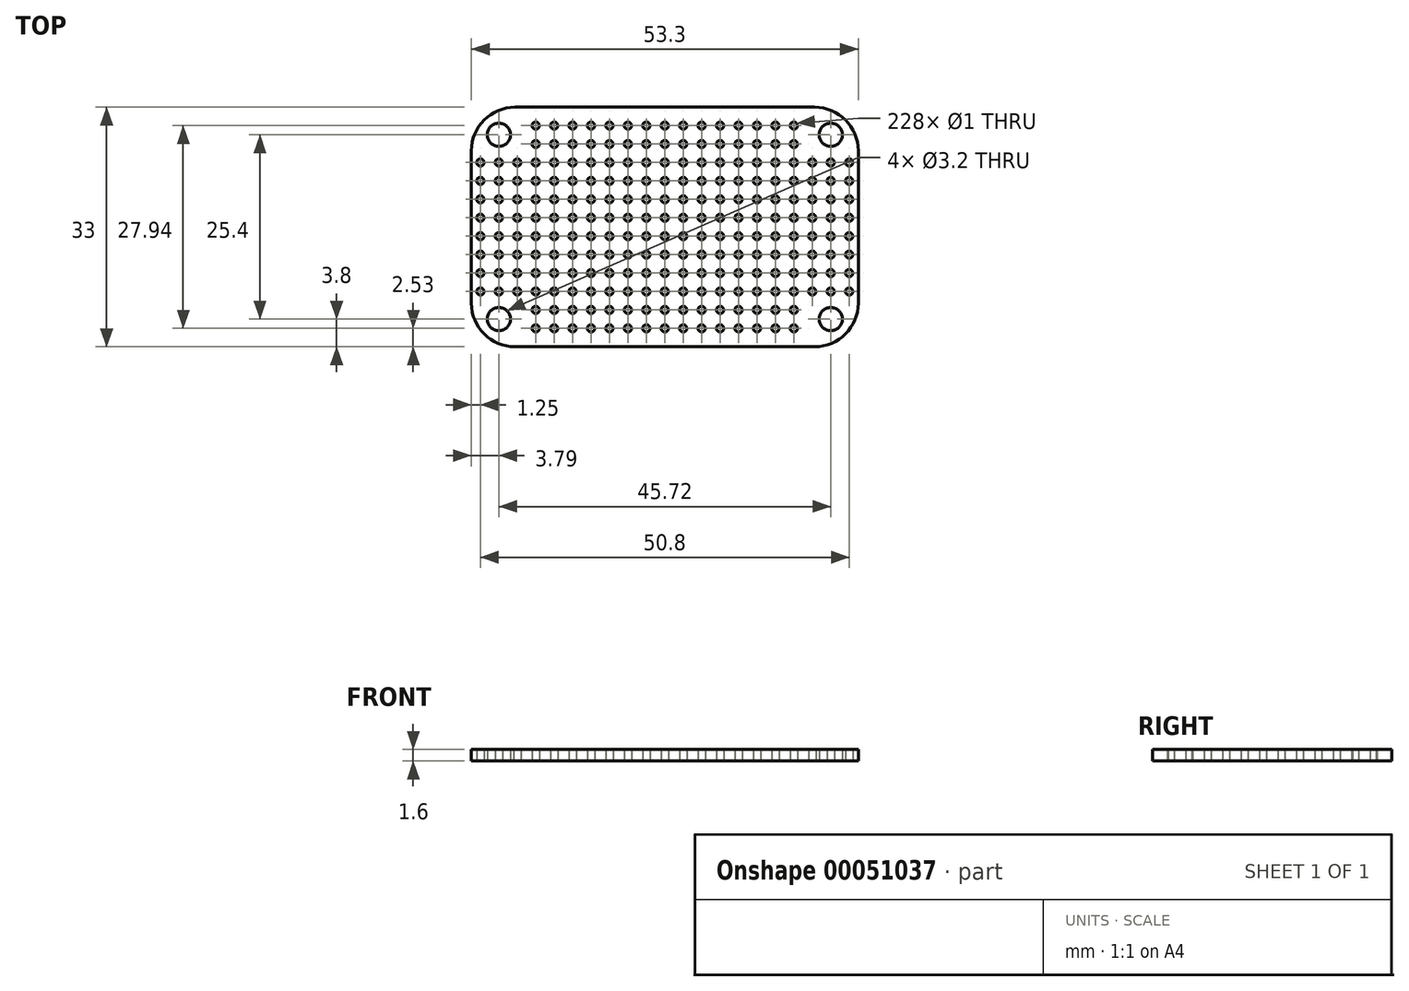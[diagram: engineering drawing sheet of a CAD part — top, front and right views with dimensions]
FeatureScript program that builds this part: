
annotation { "Feature Type Name" : "Feature", "Feature Type Description" : "" }
export const myFeature = defineFeature(function(context is Context, id is Id, definition is map)
    precondition{}
    {
        {
            var Q0;
            Q0=qCreatedBy(makeId("Top.planeOp"),FACE);
            var sketch = newSketch(context, id + "F0", { "sketchPlane" : qUnion([Q0])});
            skLineSegment(sketch, "E0.rect.bottom", {"start": v(20.65, -16.5) * mm, "end": v(-20.65, -16.5) * mm});
            skLineSegment(sketch, "E0.rect.top", {"start": v(20.65, 16.5) * mm, "end": v(-20.65, 16.5) * mm});
            skLineSegment(sketch, "E0.rect.left", {"start": v(26.65, -10.5) * mm, "end": v(26.65, 10.5) * mm});
            skLineSegment(sketch, "E0.rect.right", {"start": v(-26.65, -10.5) * mm, "end": v(-26.65, 10.5) * mm});
            skPoint(sketch, "E0.rect.middle", {"position": v(0, 0) * mm});
            skCircle(sketch, "E1.0.2.0", {"center": v(-25.4, 8.9) * mm, "radius": 0.5 * mm});
            skCircle(sketch, "E1.0.3.0", {"center": v(-25.4, 6.35) * mm, "radius": 0.5 * mm});
            skCircle(sketch, "E1.0.4.0", {"center": v(-25.4, 3.81) * mm, "radius": 0.5 * mm});
            skCircle(sketch, "E1.0.5.0", {"center": v(-25.4, 1.27) * mm, "radius": 0.5 * mm});
            skCircle(sketch, "E1.0.6.0", {"center": v(-25.4, -1.27) * mm, "radius": 0.5 * mm});
            skCircle(sketch, "E1.0.7.0", {"center": v(-25.4, -3.81) * mm, "radius": 0.5 * mm});
            skCircle(sketch, "E1.0.8.0", {"center": v(-25.4, -6.35) * mm, "radius": 0.5 * mm});
            skCircle(sketch, "E1.0.9.0", {"center": v(-25.4, -8.9) * mm, "radius": 0.5 * mm});
            skCircle(sketch, "E1.1.2.0", {"center": v(-22.86, 8.9) * mm, "radius": 0.5 * mm});
            skCircle(sketch, "E1.1.3.0", {"center": v(-22.86, 6.35) * mm, "radius": 0.5 * mm});
            skCircle(sketch, "E1.1.4.0", {"center": v(-22.86, 3.81) * mm, "radius": 0.5 * mm});
            skCircle(sketch, "E1.1.5.0", {"center": v(-22.86, 1.27) * mm, "radius": 0.5 * mm});
            skCircle(sketch, "E1.1.6.0", {"center": v(-22.86, -1.27) * mm, "radius": 0.5 * mm});
            skCircle(sketch, "E1.1.7.0", {"center": v(-22.86, -3.81) * mm, "radius": 0.5 * mm});
            skCircle(sketch, "E1.1.8.0", {"center": v(-22.86, -6.35) * mm, "radius": 0.5 * mm});
            skCircle(sketch, "E1.1.9.0", {"center": v(-22.86, -8.9) * mm, "radius": 0.5 * mm});
            skCircle(sketch, "E1.2.2.0", {"center": v(-20.32, 8.9) * mm, "radius": 0.5 * mm});
            skCircle(sketch, "E1.2.3.0", {"center": v(-20.32, 6.35) * mm, "radius": 0.5 * mm});
            skCircle(sketch, "E1.2.4.0", {"center": v(-20.32, 3.81) * mm, "radius": 0.5 * mm});
            skCircle(sketch, "E1.2.5.0", {"center": v(-20.32, 1.27) * mm, "radius": 0.5 * mm});
            skCircle(sketch, "E1.2.6.0", {"center": v(-20.32, -1.27) * mm, "radius": 0.5 * mm});
            skCircle(sketch, "E1.2.7.0", {"center": v(-20.32, -3.81) * mm, "radius": 0.5 * mm});
            skCircle(sketch, "E1.2.8.0", {"center": v(-20.32, -6.35) * mm, "radius": 0.5 * mm});
            skCircle(sketch, "E1.2.9.0", {"center": v(-20.32, -8.9) * mm, "radius": 0.5 * mm});
            skCircle(sketch, "E1.3.0.0", {"center": v(-17.78, 13.97) * mm, "radius": 0.5 * mm});
            skCircle(sketch, "E1.3.1.0", {"center": v(-17.78, 11.43) * mm, "radius": 0.5 * mm});
            skCircle(sketch, "E1.3.2.0", {"center": v(-17.78, 8.9) * mm, "radius": 0.5 * mm});
            skCircle(sketch, "E1.3.3.0", {"center": v(-17.78, 6.35) * mm, "radius": 0.5 * mm});
            skCircle(sketch, "E1.3.4.0", {"center": v(-17.78, 3.81) * mm, "radius": 0.5 * mm});
            skCircle(sketch, "E1.3.5.0", {"center": v(-17.78, 1.27) * mm, "radius": 0.5 * mm});
            skCircle(sketch, "E1.3.6.0", {"center": v(-17.78, -1.27) * mm, "radius": 0.5 * mm});
            skCircle(sketch, "E1.3.7.0", {"center": v(-17.78, -3.81) * mm, "radius": 0.5 * mm});
            skCircle(sketch, "E1.3.8.0", {"center": v(-17.78, -6.35) * mm, "radius": 0.5 * mm});
            skCircle(sketch, "E1.3.9.0", {"center": v(-17.78, -8.9) * mm, "radius": 0.5 * mm});
            skCircle(sketch, "E1.3.10.0", {"center": v(-17.78, -11.43) * mm, "radius": 0.5 * mm});
            skCircle(sketch, "E1.3.11.0", {"center": v(-17.78, -13.97) * mm, "radius": 0.5 * mm});
            skCircle(sketch, "E1.4.0.0", {"center": v(-15.24, 13.97) * mm, "radius": 0.5 * mm});
            skCircle(sketch, "E1.4.1.0", {"center": v(-15.24, 11.43) * mm, "radius": 0.5 * mm});
            skCircle(sketch, "E1.4.2.0", {"center": v(-15.24, 8.9) * mm, "radius": 0.5 * mm});
            skCircle(sketch, "E1.4.3.0", {"center": v(-15.24, 6.35) * mm, "radius": 0.5 * mm});
            skCircle(sketch, "E1.4.4.0", {"center": v(-15.24, 3.81) * mm, "radius": 0.5 * mm});
            skCircle(sketch, "E1.4.5.0", {"center": v(-15.24, 1.27) * mm, "radius": 0.5 * mm});
            skCircle(sketch, "E1.4.6.0", {"center": v(-15.24, -1.27) * mm, "radius": 0.5 * mm});
            skCircle(sketch, "E1.4.7.0", {"center": v(-15.24, -3.81) * mm, "radius": 0.5 * mm});
            skCircle(sketch, "E1.4.8.0", {"center": v(-15.24, -6.35) * mm, "radius": 0.5 * mm});
            skCircle(sketch, "E1.4.9.0", {"center": v(-15.24, -8.9) * mm, "radius": 0.5 * mm});
            skCircle(sketch, "E1.4.10.0", {"center": v(-15.24, -11.43) * mm, "radius": 0.5 * mm});
            skCircle(sketch, "E1.4.11.0", {"center": v(-15.24, -13.97) * mm, "radius": 0.5 * mm});
            skCircle(sketch, "E1.5.0.0", {"center": v(-12.7, 13.97) * mm, "radius": 0.5 * mm});
            skCircle(sketch, "E1.5.1.0", {"center": v(-12.7, 11.43) * mm, "radius": 0.5 * mm});
            skCircle(sketch, "E1.5.2.0", {"center": v(-12.7, 8.9) * mm, "radius": 0.5 * mm});
            skCircle(sketch, "E1.5.3.0", {"center": v(-12.7, 6.35) * mm, "radius": 0.5 * mm});
            skCircle(sketch, "E1.5.4.0", {"center": v(-12.7, 3.81) * mm, "radius": 0.5 * mm});
            skCircle(sketch, "E1.5.5.0", {"center": v(-12.7, 1.27) * mm, "radius": 0.5 * mm});
            skCircle(sketch, "E1.5.6.0", {"center": v(-12.7, -1.27) * mm, "radius": 0.5 * mm});
            skCircle(sketch, "E1.5.7.0", {"center": v(-12.7, -3.81) * mm, "radius": 0.5 * mm});
            skCircle(sketch, "E1.5.8.0", {"center": v(-12.7, -6.35) * mm, "radius": 0.5 * mm});
            skCircle(sketch, "E1.5.9.0", {"center": v(-12.7, -8.9) * mm, "radius": 0.5 * mm});
            skCircle(sketch, "E1.5.10.0", {"center": v(-12.7, -11.43) * mm, "radius": 0.5 * mm});
            skCircle(sketch, "E1.5.11.0", {"center": v(-12.7, -13.97) * mm, "radius": 0.5 * mm});
            skCircle(sketch, "E1.6.0.0", {"center": v(-10.16, 13.97) * mm, "radius": 0.5 * mm});
            skCircle(sketch, "E1.6.1.0", {"center": v(-10.16, 11.43) * mm, "radius": 0.5 * mm});
            skCircle(sketch, "E1.6.2.0", {"center": v(-10.16, 8.9) * mm, "radius": 0.5 * mm});
            skCircle(sketch, "E1.6.3.0", {"center": v(-10.16, 6.35) * mm, "radius": 0.5 * mm});
            skCircle(sketch, "E1.6.4.0", {"center": v(-10.16, 3.81) * mm, "radius": 0.5 * mm});
            skCircle(sketch, "E1.6.5.0", {"center": v(-10.16, 1.27) * mm, "radius": 0.5 * mm});
            skCircle(sketch, "E1.6.6.0", {"center": v(-10.16, -1.27) * mm, "radius": 0.5 * mm});
            skCircle(sketch, "E1.6.7.0", {"center": v(-10.16, -3.81) * mm, "radius": 0.5 * mm});
            skCircle(sketch, "E1.6.8.0", {"center": v(-10.16, -6.35) * mm, "radius": 0.5 * mm});
            skCircle(sketch, "E1.6.9.0", {"center": v(-10.16, -8.9) * mm, "radius": 0.5 * mm});
            skCircle(sketch, "E1.6.10.0", {"center": v(-10.16, -11.43) * mm, "radius": 0.5 * mm});
            skCircle(sketch, "E1.6.11.0", {"center": v(-10.16, -13.97) * mm, "radius": 0.5 * mm});
            skCircle(sketch, "E1.7.0.0", {"center": v(-7.62, 13.97) * mm, "radius": 0.5 * mm});
            skCircle(sketch, "E1.7.1.0", {"center": v(-7.62, 11.43) * mm, "radius": 0.5 * mm});
            skCircle(sketch, "E1.7.2.0", {"center": v(-7.62, 8.9) * mm, "radius": 0.5 * mm});
            skCircle(sketch, "E1.7.3.0", {"center": v(-7.62, 6.35) * mm, "radius": 0.5 * mm});
            skCircle(sketch, "E1.7.4.0", {"center": v(-7.62, 3.81) * mm, "radius": 0.5 * mm});
            skCircle(sketch, "E1.7.5.0", {"center": v(-7.62, 1.27) * mm, "radius": 0.5 * mm});
            skCircle(sketch, "E1.7.6.0", {"center": v(-7.62, -1.27) * mm, "radius": 0.5 * mm});
            skCircle(sketch, "E1.7.7.0", {"center": v(-7.62, -3.81) * mm, "radius": 0.5 * mm});
            skCircle(sketch, "E1.7.8.0", {"center": v(-7.62, -6.35) * mm, "radius": 0.5 * mm});
            skCircle(sketch, "E1.7.9.0", {"center": v(-7.62, -8.9) * mm, "radius": 0.5 * mm});
            skCircle(sketch, "E1.7.10.0", {"center": v(-7.62, -11.43) * mm, "radius": 0.5 * mm});
            skCircle(sketch, "E1.7.11.0", {"center": v(-7.62, -13.97) * mm, "radius": 0.5 * mm});
            skCircle(sketch, "E1.8.0.0", {"center": v(-5.08, 13.97) * mm, "radius": 0.5 * mm});
            skCircle(sketch, "E1.8.1.0", {"center": v(-5.08, 11.43) * mm, "radius": 0.5 * mm});
            skCircle(sketch, "E1.8.2.0", {"center": v(-5.08, 8.9) * mm, "radius": 0.5 * mm});
            skCircle(sketch, "E1.8.3.0", {"center": v(-5.08, 6.35) * mm, "radius": 0.5 * mm});
            skCircle(sketch, "E1.8.4.0", {"center": v(-5.08, 3.81) * mm, "radius": 0.5 * mm});
            skCircle(sketch, "E1.8.5.0", {"center": v(-5.08, 1.27) * mm, "radius": 0.5 * mm});
            skCircle(sketch, "E1.8.6.0", {"center": v(-5.08, -1.27) * mm, "radius": 0.5 * mm});
            skCircle(sketch, "E1.8.7.0", {"center": v(-5.08, -3.81) * mm, "radius": 0.5 * mm});
            skCircle(sketch, "E1.8.8.0", {"center": v(-5.08, -6.35) * mm, "radius": 0.5 * mm});
            skCircle(sketch, "E1.8.9.0", {"center": v(-5.08, -8.9) * mm, "radius": 0.5 * mm});
            skCircle(sketch, "E1.8.10.0", {"center": v(-5.08, -11.43) * mm, "radius": 0.5 * mm});
            skCircle(sketch, "E1.8.11.0", {"center": v(-5.08, -13.97) * mm, "radius": 0.5 * mm});
            skCircle(sketch, "E1.9.0.0", {"center": v(-2.54, 13.97) * mm, "radius": 0.5 * mm});
            skCircle(sketch, "E1.9.1.0", {"center": v(-2.54, 11.43) * mm, "radius": 0.5 * mm});
            skCircle(sketch, "E1.9.2.0", {"center": v(-2.54, 8.9) * mm, "radius": 0.5 * mm});
            skCircle(sketch, "E1.9.3.0", {"center": v(-2.54, 6.35) * mm, "radius": 0.5 * mm});
            skCircle(sketch, "E1.9.4.0", {"center": v(-2.54, 3.81) * mm, "radius": 0.5 * mm});
            skCircle(sketch, "E1.9.5.0", {"center": v(-2.54, 1.27) * mm, "radius": 0.5 * mm});
            skCircle(sketch, "E1.9.6.0", {"center": v(-2.54, -1.27) * mm, "radius": 0.5 * mm});
            skCircle(sketch, "E1.9.7.0", {"center": v(-2.54, -3.81) * mm, "radius": 0.5 * mm});
            skCircle(sketch, "E1.9.8.0", {"center": v(-2.54, -6.35) * mm, "radius": 0.5 * mm});
            skCircle(sketch, "E1.9.9.0", {"center": v(-2.54, -8.9) * mm, "radius": 0.5 * mm});
            skCircle(sketch, "E1.9.10.0", {"center": v(-2.54, -11.43) * mm, "radius": 0.5 * mm});
            skCircle(sketch, "E1.9.11.0", {"center": v(-2.54, -13.97) * mm, "radius": 0.5 * mm});
            skCircle(sketch, "E1.10.0.0", {"center": v(0, 13.97) * mm, "radius": 0.5 * mm});
            skCircle(sketch, "E1.10.1.0", {"center": v(0, 11.43) * mm, "radius": 0.5 * mm});
            skCircle(sketch, "E1.10.2.0", {"center": v(0, 8.9) * mm, "radius": 0.5 * mm});
            skCircle(sketch, "E1.10.3.0", {"center": v(0, 6.35) * mm, "radius": 0.5 * mm});
            skCircle(sketch, "E1.10.4.0", {"center": v(0, 3.81) * mm, "radius": 0.5 * mm});
            skCircle(sketch, "E1.10.5.0", {"center": v(0, 1.27) * mm, "radius": 0.5 * mm});
            skCircle(sketch, "E1.10.6.0", {"center": v(0, -1.27) * mm, "radius": 0.5 * mm});
            skCircle(sketch, "E1.10.7.0", {"center": v(0, -3.81) * mm, "radius": 0.5 * mm});
            skCircle(sketch, "E1.10.8.0", {"center": v(0, -6.35) * mm, "radius": 0.5 * mm});
            skCircle(sketch, "E1.10.9.0", {"center": v(0, -8.9) * mm, "radius": 0.5 * mm});
            skCircle(sketch, "E1.10.10.0", {"center": v(0, -11.43) * mm, "radius": 0.5 * mm});
            skCircle(sketch, "E1.10.11.0", {"center": v(0, -13.97) * mm, "radius": 0.5 * mm});
            skCircle(sketch, "E1.11.0.0", {"center": v(2.54, 13.97) * mm, "radius": 0.5 * mm});
            skCircle(sketch, "E1.11.1.0", {"center": v(2.54, 11.43) * mm, "radius": 0.5 * mm});
            skCircle(sketch, "E1.11.2.0", {"center": v(2.54, 8.9) * mm, "radius": 0.5 * mm});
            skCircle(sketch, "E1.11.3.0", {"center": v(2.54, 6.35) * mm, "radius": 0.5 * mm});
            skCircle(sketch, "E1.11.4.0", {"center": v(2.54, 3.81) * mm, "radius": 0.5 * mm});
            skCircle(sketch, "E1.11.5.0", {"center": v(2.54, 1.27) * mm, "radius": 0.5 * mm});
            skCircle(sketch, "E1.11.6.0", {"center": v(2.54, -1.27) * mm, "radius": 0.5 * mm});
            skCircle(sketch, "E1.11.7.0", {"center": v(2.54, -3.81) * mm, "radius": 0.5 * mm});
            skCircle(sketch, "E1.11.8.0", {"center": v(2.54, -6.35) * mm, "radius": 0.5 * mm});
            skCircle(sketch, "E1.11.9.0", {"center": v(2.54, -8.9) * mm, "radius": 0.5 * mm});
            skCircle(sketch, "E1.11.10.0", {"center": v(2.54, -11.43) * mm, "radius": 0.5 * mm});
            skCircle(sketch, "E1.11.11.0", {"center": v(2.54, -13.97) * mm, "radius": 0.5 * mm});
            skCircle(sketch, "E1.12.0.0", {"center": v(5.08, 13.97) * mm, "radius": 0.5 * mm});
            skCircle(sketch, "E1.12.1.0", {"center": v(5.08, 11.43) * mm, "radius": 0.5 * mm});
            skCircle(sketch, "E1.12.2.0", {"center": v(5.08, 8.9) * mm, "radius": 0.5 * mm});
            skCircle(sketch, "E1.12.3.0", {"center": v(5.08, 6.35) * mm, "radius": 0.5 * mm});
            skCircle(sketch, "E1.12.4.0", {"center": v(5.08, 3.81) * mm, "radius": 0.5 * mm});
            skCircle(sketch, "E1.12.5.0", {"center": v(5.08, 1.27) * mm, "radius": 0.5 * mm});
            skCircle(sketch, "E1.12.6.0", {"center": v(5.08, -1.27) * mm, "radius": 0.5 * mm});
            skCircle(sketch, "E1.12.7.0", {"center": v(5.08, -3.81) * mm, "radius": 0.5 * mm});
            skCircle(sketch, "E1.12.8.0", {"center": v(5.08, -6.35) * mm, "radius": 0.5 * mm});
            skCircle(sketch, "E1.12.9.0", {"center": v(5.08, -8.9) * mm, "radius": 0.5 * mm});
            skCircle(sketch, "E1.12.10.0", {"center": v(5.08, -11.43) * mm, "radius": 0.5 * mm});
            skCircle(sketch, "E1.12.11.0", {"center": v(5.08, -13.97) * mm, "radius": 0.5 * mm});
            skCircle(sketch, "E1.13.0.0", {"center": v(7.62, 13.97) * mm, "radius": 0.5 * mm});
            skCircle(sketch, "E1.13.1.0", {"center": v(7.62, 11.43) * mm, "radius": 0.5 * mm});
            skCircle(sketch, "E1.13.2.0", {"center": v(7.62, 8.9) * mm, "radius": 0.5 * mm});
            skCircle(sketch, "E1.13.3.0", {"center": v(7.62, 6.35) * mm, "radius": 0.5 * mm});
            skCircle(sketch, "E1.13.4.0", {"center": v(7.62, 3.81) * mm, "radius": 0.5 * mm});
            skCircle(sketch, "E1.13.5.0", {"center": v(7.62, 1.27) * mm, "radius": 0.5 * mm});
            skCircle(sketch, "E1.13.6.0", {"center": v(7.62, -1.27) * mm, "radius": 0.5 * mm});
            skCircle(sketch, "E1.13.7.0", {"center": v(7.62, -3.81) * mm, "radius": 0.5 * mm});
            skCircle(sketch, "E1.13.8.0", {"center": v(7.62, -6.35) * mm, "radius": 0.5 * mm});
            skCircle(sketch, "E1.13.9.0", {"center": v(7.62, -8.9) * mm, "radius": 0.5 * mm});
            skCircle(sketch, "E1.13.10.0", {"center": v(7.62, -11.43) * mm, "radius": 0.5 * mm});
            skCircle(sketch, "E1.13.11.0", {"center": v(7.62, -13.97) * mm, "radius": 0.5 * mm});
            skCircle(sketch, "E1.14.0.0", {"center": v(10.16, 13.97) * mm, "radius": 0.5 * mm});
            skCircle(sketch, "E1.14.1.0", {"center": v(10.16, 11.43) * mm, "radius": 0.5 * mm});
            skCircle(sketch, "E1.14.2.0", {"center": v(10.16, 8.9) * mm, "radius": 0.5 * mm});
            skCircle(sketch, "E1.14.3.0", {"center": v(10.16, 6.35) * mm, "radius": 0.5 * mm});
            skCircle(sketch, "E1.14.4.0", {"center": v(10.16, 3.81) * mm, "radius": 0.5 * mm});
            skCircle(sketch, "E1.14.5.0", {"center": v(10.16, 1.27) * mm, "radius": 0.5 * mm});
            skCircle(sketch, "E1.14.6.0", {"center": v(10.16, -1.27) * mm, "radius": 0.5 * mm});
            skCircle(sketch, "E1.14.7.0", {"center": v(10.16, -3.81) * mm, "radius": 0.5 * mm});
            skCircle(sketch, "E1.14.8.0", {"center": v(10.16, -6.35) * mm, "radius": 0.5 * mm});
            skCircle(sketch, "E1.14.9.0", {"center": v(10.16, -8.9) * mm, "radius": 0.5 * mm});
            skCircle(sketch, "E1.14.10.0", {"center": v(10.16, -11.43) * mm, "radius": 0.5 * mm});
            skCircle(sketch, "E1.14.11.0", {"center": v(10.16, -13.97) * mm, "radius": 0.5 * mm});
            skCircle(sketch, "E1.15.0.0", {"center": v(12.7, 13.97) * mm, "radius": 0.5 * mm});
            skCircle(sketch, "E1.15.1.0", {"center": v(12.7, 11.43) * mm, "radius": 0.5 * mm});
            skCircle(sketch, "E1.15.2.0", {"center": v(12.7, 8.9) * mm, "radius": 0.5 * mm});
            skCircle(sketch, "E1.15.3.0", {"center": v(12.7, 6.35) * mm, "radius": 0.5 * mm});
            skCircle(sketch, "E1.15.4.0", {"center": v(12.7, 3.81) * mm, "radius": 0.5 * mm});
            skCircle(sketch, "E1.15.5.0", {"center": v(12.7, 1.27) * mm, "radius": 0.5 * mm});
            skCircle(sketch, "E1.15.6.0", {"center": v(12.7, -1.27) * mm, "radius": 0.5 * mm});
            skCircle(sketch, "E1.15.7.0", {"center": v(12.7, -3.81) * mm, "radius": 0.5 * mm});
            skCircle(sketch, "E1.15.8.0", {"center": v(12.7, -6.35) * mm, "radius": 0.5 * mm});
            skCircle(sketch, "E1.15.9.0", {"center": v(12.7, -8.9) * mm, "radius": 0.5 * mm});
            skCircle(sketch, "E1.15.10.0", {"center": v(12.7, -11.43) * mm, "radius": 0.5 * mm});
            skCircle(sketch, "E1.15.11.0", {"center": v(12.7, -13.97) * mm, "radius": 0.5 * mm});
            skCircle(sketch, "E1.16.0.0", {"center": v(15.24, 13.97) * mm, "radius": 0.5 * mm});
            skCircle(sketch, "E1.16.1.0", {"center": v(15.24, 11.43) * mm, "radius": 0.5 * mm});
            skCircle(sketch, "E1.16.2.0", {"center": v(15.24, 8.9) * mm, "radius": 0.5 * mm});
            skCircle(sketch, "E1.16.3.0", {"center": v(15.24, 6.35) * mm, "radius": 0.5 * mm});
            skCircle(sketch, "E1.16.4.0", {"center": v(15.24, 3.81) * mm, "radius": 0.5 * mm});
            skCircle(sketch, "E1.16.5.0", {"center": v(15.24, 1.27) * mm, "radius": 0.5 * mm});
            skCircle(sketch, "E1.16.6.0", {"center": v(15.24, -1.27) * mm, "radius": 0.5 * mm});
            skCircle(sketch, "E1.16.7.0", {"center": v(15.24, -3.81) * mm, "radius": 0.5 * mm});
            skCircle(sketch, "E1.16.8.0", {"center": v(15.24, -6.35) * mm, "radius": 0.5 * mm});
            skCircle(sketch, "E1.16.9.0", {"center": v(15.24, -8.9) * mm, "radius": 0.5 * mm});
            skCircle(sketch, "E1.16.10.0", {"center": v(15.24, -11.43) * mm, "radius": 0.5 * mm});
            skCircle(sketch, "E1.16.11.0", {"center": v(15.24, -13.97) * mm, "radius": 0.5 * mm});
            skCircle(sketch, "E1.17.0.0", {"center": v(17.78, 13.97) * mm, "radius": 0.5 * mm});
            skCircle(sketch, "E1.17.1.0", {"center": v(17.78, 11.43) * mm, "radius": 0.5 * mm});
            skCircle(sketch, "E1.17.2.0", {"center": v(17.78, 8.9) * mm, "radius": 0.5 * mm});
            skCircle(sketch, "E1.17.3.0", {"center": v(17.78, 6.35) * mm, "radius": 0.5 * mm});
            skCircle(sketch, "E1.17.4.0", {"center": v(17.78, 3.81) * mm, "radius": 0.5 * mm});
            skCircle(sketch, "E1.17.5.0", {"center": v(17.78, 1.27) * mm, "radius": 0.5 * mm});
            skCircle(sketch, "E1.17.6.0", {"center": v(17.78, -1.27) * mm, "radius": 0.5 * mm});
            skCircle(sketch, "E1.17.7.0", {"center": v(17.78, -3.81) * mm, "radius": 0.5 * mm});
            skCircle(sketch, "E1.17.8.0", {"center": v(17.78, -6.35) * mm, "radius": 0.5 * mm});
            skCircle(sketch, "E1.17.9.0", {"center": v(17.78, -8.9) * mm, "radius": 0.5 * mm});
            skCircle(sketch, "E1.17.10.0", {"center": v(17.78, -11.43) * mm, "radius": 0.5 * mm});
            skCircle(sketch, "E1.17.11.0", {"center": v(17.78, -13.97) * mm, "radius": 0.5 * mm});
            skCircle(sketch, "E1.18.2.0", {"center": v(20.32, 8.9) * mm, "radius": 0.5 * mm});
            skCircle(sketch, "E1.18.3.0", {"center": v(20.32, 6.35) * mm, "radius": 0.5 * mm});
            skCircle(sketch, "E1.18.4.0", {"center": v(20.32, 3.81) * mm, "radius": 0.5 * mm});
            skCircle(sketch, "E1.18.5.0", {"center": v(20.32, 1.27) * mm, "radius": 0.5 * mm});
            skCircle(sketch, "E1.18.6.0", {"center": v(20.32, -1.27) * mm, "radius": 0.5 * mm});
            skCircle(sketch, "E1.18.7.0", {"center": v(20.32, -3.81) * mm, "radius": 0.5 * mm});
            skCircle(sketch, "E1.18.8.0", {"center": v(20.32, -6.35) * mm, "radius": 0.5 * mm});
            skCircle(sketch, "E1.18.9.0", {"center": v(20.32, -8.9) * mm, "radius": 0.5 * mm});
            skCircle(sketch, "E1.19.2.0", {"center": v(22.86, 8.9) * mm, "radius": 0.5 * mm});
            skCircle(sketch, "E1.19.3.0", {"center": v(22.86, 6.35) * mm, "radius": 0.5 * mm});
            skCircle(sketch, "E1.19.4.0", {"center": v(22.86, 3.81) * mm, "radius": 0.5 * mm});
            skCircle(sketch, "E1.19.5.0", {"center": v(22.86, 1.27) * mm, "radius": 0.5 * mm});
            skCircle(sketch, "E1.19.6.0", {"center": v(22.86, -1.27) * mm, "radius": 0.5 * mm});
            skCircle(sketch, "E1.19.7.0", {"center": v(22.86, -3.81) * mm, "radius": 0.5 * mm});
            skCircle(sketch, "E1.19.8.0", {"center": v(22.86, -6.35) * mm, "radius": 0.5 * mm});
            skCircle(sketch, "E1.19.9.0", {"center": v(22.86, -8.9) * mm, "radius": 0.5 * mm});
            skCircle(sketch, "E1.20.2.0", {"center": v(25.4, 8.9) * mm, "radius": 0.5 * mm});
            skCircle(sketch, "E1.20.3.0", {"center": v(25.4, 6.35) * mm, "radius": 0.5 * mm});
            skCircle(sketch, "E1.20.4.0", {"center": v(25.4, 3.81) * mm, "radius": 0.5 * mm});
            skCircle(sketch, "E1.20.5.0", {"center": v(25.4, 1.27) * mm, "radius": 0.5 * mm});
            skCircle(sketch, "E1.20.6.0", {"center": v(25.4, -1.27) * mm, "radius": 0.5 * mm});
            skCircle(sketch, "E1.20.7.0", {"center": v(25.4, -3.81) * mm, "radius": 0.5 * mm});
            skCircle(sketch, "E1.20.8.0", {"center": v(25.4, -6.35) * mm, "radius": 0.5 * mm});
            skCircle(sketch, "E1.20.9.0", {"center": v(25.4, -8.9) * mm, "radius": 0.5 * mm});
            skLineSegment(sketch, "E1.direction1", {"start": v(-25.4, 13.97) * mm, "end": v(-22.86, 13.97) * mm, "construction": true});
            skLineSegment(sketch, "E1.direction2", {"start": v(-25.4, 13.97) * mm, "end": v(-25.4, 11.43) * mm, "construction": true});
            skLineSegment(sketch, "E2", {"start": v(-26.65, 0) * mm, "end": v(26.65, 0) * mm, "construction": true});
            skLineSegment(sketch, "E3", {"start": v(0, 16.5) * mm, "end": v(0, -16.5) * mm, "construction": true});
            skCircle(sketch, "E4", {"center": v(-22.86, -12.7) * mm, "radius": 1.6 * mm});
            skCircle(sketch, "E5.0.1.0", {"center": v(-22.86, 12.7) * mm, "radius": 1.6 * mm});
            skCircle(sketch, "E5.1.0.0", {"center": v(22.86, -12.7) * mm, "radius": 1.6 * mm});
            skCircle(sketch, "E5.1.1.0", {"center": v(22.86, 12.7) * mm, "radius": 1.6 * mm});
            skLineSegment(sketch, "E5.direction1", {"start": v(-22.86, -12.7) * mm, "end": v(22.86, -12.7) * mm, "construction": true});
            skLineSegment(sketch, "E5.direction2", {"start": v(-22.86, -12.7) * mm, "end": v(-22.86, 12.7) * mm, "construction": true});
            skPoint(sketch, "E6.visualSharp", {"position": v(-26.65, 16.5) * mm});
            skArc(sketch, "E6.filletArc", {"start": v(-20.65, 16.5) * mm, "mid": v(-24.9, 14.74) * mm, "end": v(-26.65, 10.5) * mm});
            skPoint(sketch, "E7.visualSharp", {"position": v(26.65, 16.5) * mm});
            skArc(sketch, "E7.filletArc", {"start": v(26.65, 10.5) * mm, "mid": v(24.9, 14.74) * mm, "end": v(20.65, 16.5) * mm});
            skPoint(sketch, "E8.visualSharp", {"position": v(26.65, -16.5) * mm});
            skArc(sketch, "E8.filletArc", {"start": v(20.65, -16.5) * mm, "mid": v(24.9, -14.74) * mm, "end": v(26.65, -10.5) * mm});
            skPoint(sketch, "E9.visualSharp", {"position": v(-26.65, -16.5) * mm});
            skArc(sketch, "E9.filletArc", {"start": v(-26.65, -10.5) * mm, "mid": v(-24.9, -14.74) * mm, "end": v(-20.65, -16.5) * mm});
            skSolve(sketch);
        }
        {
            var Q0;
            Q0=makeQuery(id+"F0.imprint","IMPRINT",FACE,{"disambiguationData":[TD([[makeQuery(id+"F0.imprint","IMPRINT",EDGE,{"derivedFrom":sQuery(id+"F0.wireOp",EDGE,"E0.rect.bottom")}),-1.0]])]});
            extrude(context, id + "F1", {"entities" : qUnion([Q0]), "depth" : 1.6 * mm});
        }
    });
